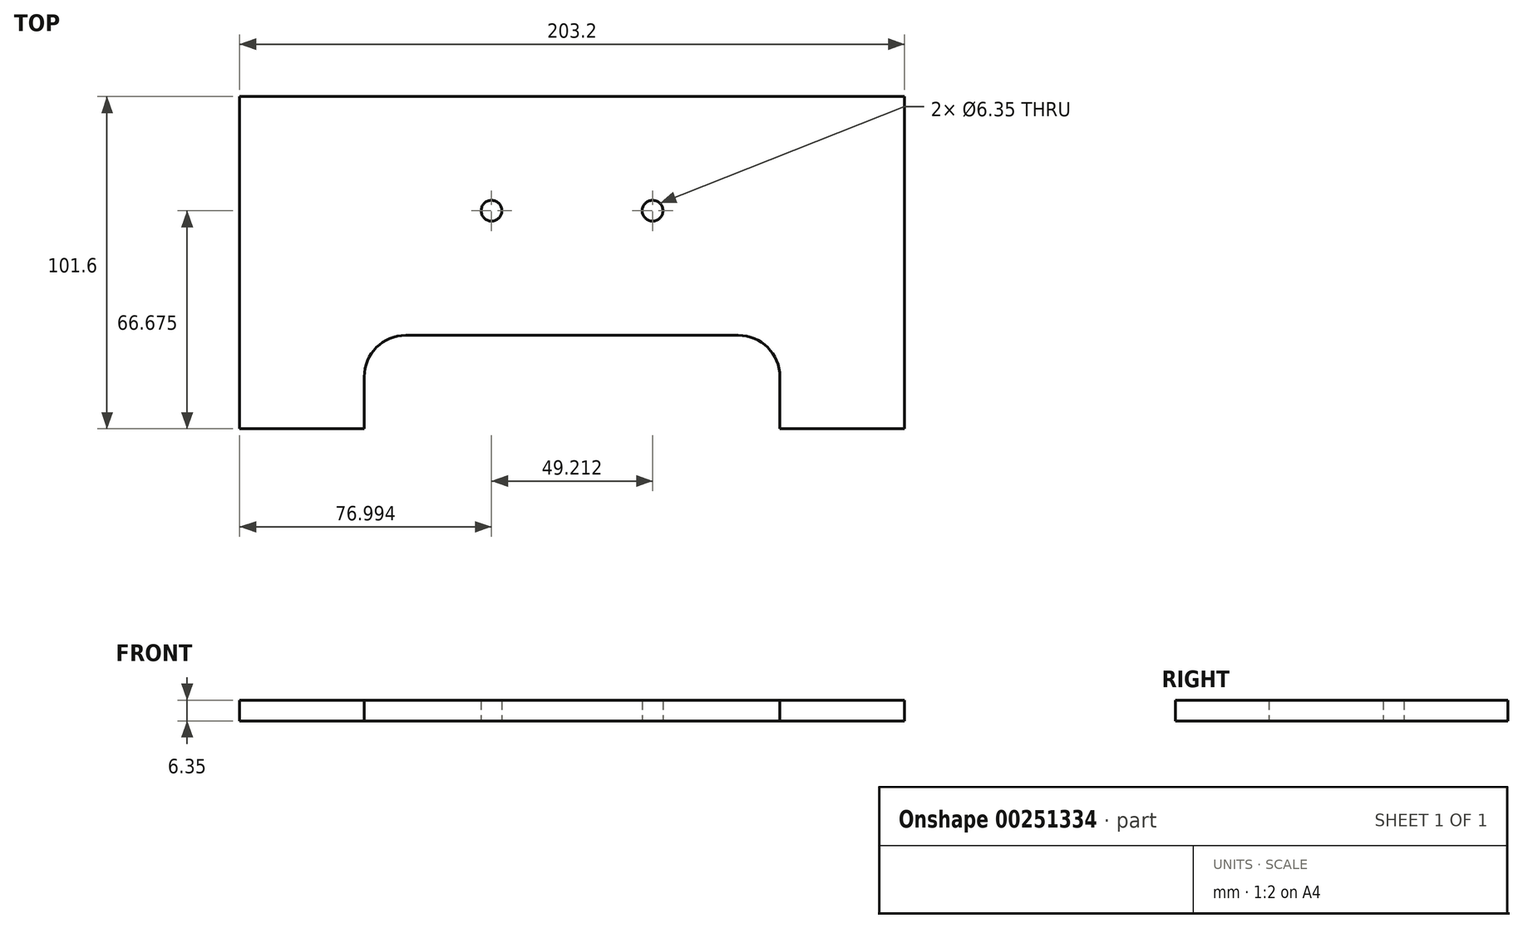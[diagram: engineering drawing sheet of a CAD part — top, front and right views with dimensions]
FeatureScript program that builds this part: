
annotation { "Feature Type Name" : "Feature", "Feature Type Description" : "" }
export const myFeature = defineFeature(function(context is Context, id is Id, definition is map)
    precondition{}
    {
        {
            var Q0;
            Q0=qCreatedBy(makeId("Top.planeOp"),FACE);
            var sketch = newSketch(context, id + "F0", { "sketchPlane" : qUnion([Q0])});
            skLineSegment(sketch, "E0.bottom", {"start": v(-101.6, 101.6) * mm, "end": v(101.6, 101.6) * mm});
            skLineSegment(sketch, "E0.top", {"start": v(-101.6, 0) * mm, "end": v(101.6, 0) * mm});
            skLineSegment(sketch, "E0.left", {"start": v(-101.6, 101.6) * mm, "end": v(-101.6, 0) * mm});
            skLineSegment(sketch, "E0.right", {"start": v(101.6, 101.6) * mm, "end": v(101.6, 0) * mm});
            skLineSegment(sketch, "E1.bottom", {"start": v(-63.5, 28.57) * mm, "end": v(63.5, 28.57) * mm});
            skLineSegment(sketch, "E1.top", {"start": v(-63.5, 0) * mm, "end": v(63.5, 0) * mm});
            skLineSegment(sketch, "E1.left", {"start": v(-63.5, 28.57) * mm, "end": v(-63.5, 0) * mm});
            skLineSegment(sketch, "E1.right", {"start": v(63.5, 28.57) * mm, "end": v(63.5, 0) * mm});
            skLineSegment(sketch, "E2", {"start": v(0, 0) * mm, "end": v(0, 144.8) * mm});
            skCircle(sketch, "E3", {"center": v(-24.6, 66.67) * mm, "radius": 3.18 * mm});
            skCircle(sketch, "E4.MirrorC", {"center": v(24.6, 66.67) * mm, "radius": 3.18 * mm});
            skSolve(sketch);
        }
        {
            var Q0;
            {var subQ4=sQuery(id+"F0.wireOp",EDGE,"E0.left");Q0=makeQuery(id+"F0.imprint","IMPRINT",FACE,{"disambiguationData":[TD([[makeQuery(id+"F0.imprint","IMPRINT",EDGE,{"derivedFrom":subQ4}),1.0]])]});}
            var Q1;
            {var subQ4=sQuery(id+"F0.wireOp",EDGE,"E0.right");Q1=makeQuery(id+"F0.imprint","IMPRINT",FACE,{"disambiguationData":[TD([[makeQuery(id+"F0.imprint","IMPRINT",EDGE,{"derivedFrom":subQ4}),-1.0]])]});}
            extrude(context, id + "F1", {"entities" : qUnion([Q0, Q1]), "depth" : 6.35 * mm});
        }
        {
            var Q0;
            Q0=makeQuery(id+"F1.opExtrude","SWEPT_EDGE",EDGE,{"disambiguationData":[OSD([sQuery(id+"F0.wireOp",EDGE,"E1.bottom"),sQuery(id+"F0.wireOp",EDGE,"E1.left")])]});
            var Q1;
            Q1=makeQuery(id+"F1.opExtrude","SWEPT_EDGE",EDGE,{"disambiguationData":[OSD([sQuery(id+"F0.wireOp",EDGE,"E1.bottom"),sQuery(id+"F0.wireOp",EDGE,"E1.right")])]});
            fillet(context, id + "F2", {"entities" : qUnion([Q0, Q1]), "radius" : 12.7 * mm, "tangentPropagation" : true, "allowEdgeOverflow" : false});
        }
    });
